# Revit family: protivipozarnae_stora_firetechnics-s_garmoshka
name_source: partatom
category: Двери
revit_build: Autodesk Revit 2018 (Build: 20170223_1515(x64)
units: mm (PartAtom-declared; Revit-internal decimal feet)

## family parameters
Всегда вертикально = Да
На основе рабочей плоскости = Нет
Общий = Нет
При загрузке вырезать с полостями = Нет
Точка расчета площади = Нет

## types (1)
- Противопожарные шторы FireTechnics-S «Гармошка»
    ADSK_URL страницы изделия = https://www.fire-tec.ru
    ADSK_Завод-изготовитель = Firetechnics
    ADSK_Наименование = Протипожарная штора Firetechnics-S "Гармошка" EI120
    ADSK_Предел огнестойкости = EI120
    ADSK_Размер_Высота = 5000 мм
    ADSK_Размер_Длина = 2000 мм
    ADSK_Размер_Ширина = 4000 мм
    URL = https://www.fire-tec.ru
    Аналитическая конструкция = <Нет>
    Внутренняя длина = 1400 мм
    Внутренняя ширина = 3400 мм
    Высота верхнего короба = 200 мм
    Высота нижнего короба = 100 мм
    Изготовитель = Firetechnics
    Материал короба = Сталь_оцинкованная_листовая_1мм_Firetechnics
    Материал полотна = Полотно
    ширина короба = 300 мм

## geometry (parser evidence)
native form markers: Blend x2
no freeform markers — native parametric forms only
